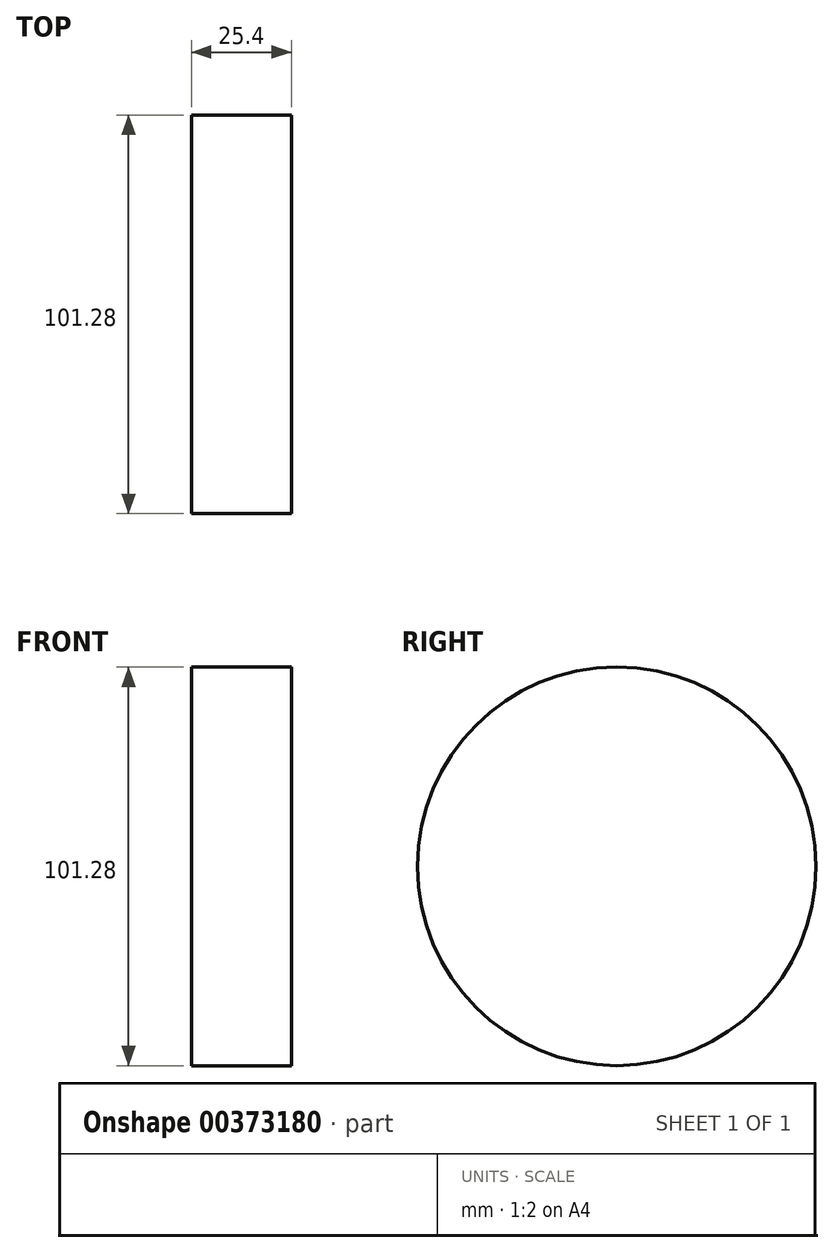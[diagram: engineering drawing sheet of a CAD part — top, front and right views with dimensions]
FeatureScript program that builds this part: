
annotation { "Feature Type Name" : "Feature", "Feature Type Description" : "" }
export const myFeature = defineFeature(function(context is Context, id is Id, definition is map)
    precondition{}
    {
        {
            var Q0;
            Q0=qCreatedBy(makeId("Right.planeOp"),FACE);
            var sketch = newSketch(context, id + "F0", { "sketchPlane" : qUnion([Q0])});
            skCircle(sketch, "E0", {"center": v(0, 0) * mm, "radius": 50.64 * mm});
            skSolve(sketch);
        }
        {
            var Q0;
            Q0 = qSketchRegion(id + "F0", true);
            extrude(context, id + "F1", {"entities" : qUnion([Q0]), "depth" : 25.4 * mm});
        }
    });
